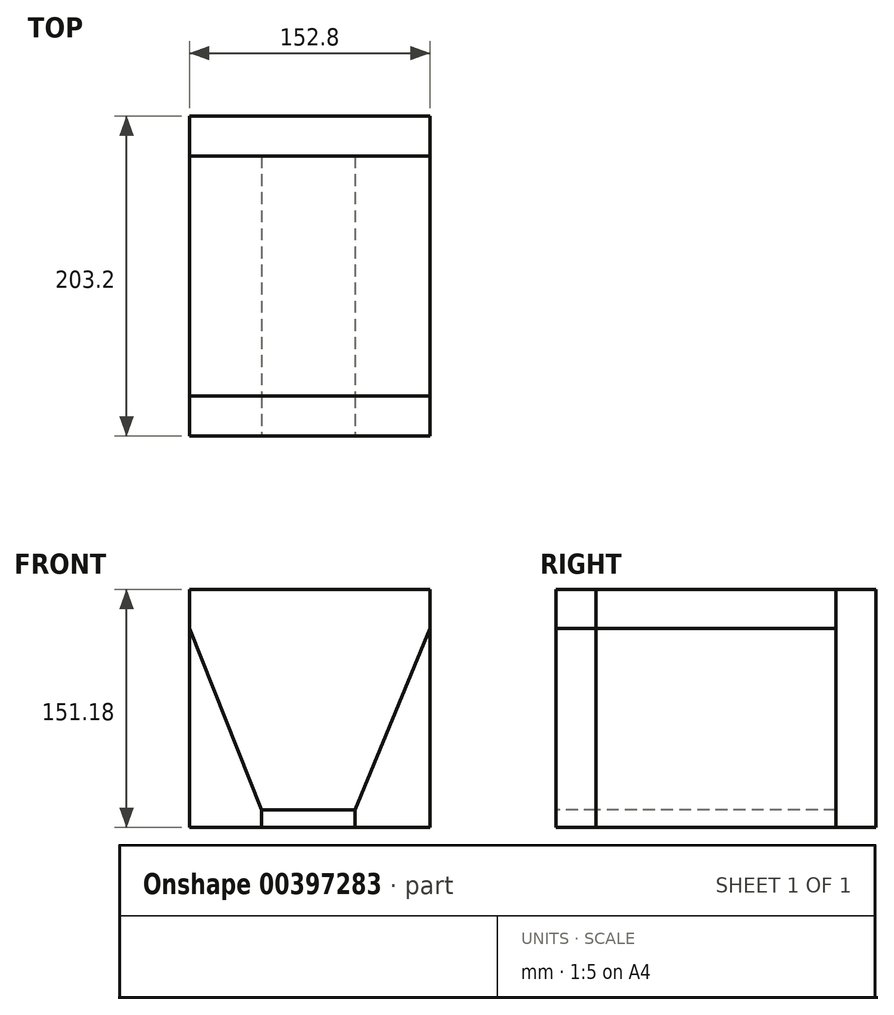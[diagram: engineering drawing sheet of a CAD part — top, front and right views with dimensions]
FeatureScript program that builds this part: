
annotation { "Feature Type Name" : "Feature", "Feature Type Description" : "" }
export const myFeature = defineFeature(function(context is Context, id is Id, definition is map)
    precondition{}
    {
        {
            var Q0;
            Q0=qCreatedBy(makeId("Front.planeOp"),FACE);
            var sketch = newSketch(context, id + "F0", { "sketchPlane" : qUnion([Q0])});
            skLineSegment(sketch, "E0.bottom", {"start": v(-76.38, 75.79) * mm, "end": v(76.38, 75.79) * mm});
            skLineSegment(sketch, "E0.top", {"start": v(-76.38, -75.4) * mm, "end": v(76.38, -75.4) * mm});
            skLineSegment(sketch, "E0.left", {"start": v(-76.38, 75.79) * mm, "end": v(-76.38, -75.4) * mm});
            skLineSegment(sketch, "E0.right", {"start": v(76.38, 75.79) * mm, "end": v(76.38, -75.4) * mm});
            skSolve(sketch);
        }
        {
            var Q0;
            Q0=makeQuery(id+"F0.imprint","IMPRINT",FACE,{"disambiguationData":[TD([[makeQuery(id+"F0.imprint","IMPRINT",EDGE,{"derivedFrom":sQuery(id+"F0.wireOp",EDGE,"E0.bottom")}),-1.0]])]});
            extrude(context, id + "F1", {"entities" : qUnion([Q0]), "depth" : 152.4 * mm});
        }
        {
            var Q0;
            Q0=makeQuery(id+"F1.opExtrude","CAP_FACE",FACE,{"disambiguationData":[OSD([sQuery(id+"F0.wireOp",EDGE,"E0.bottom"),sQuery(id+"F0.wireOp",EDGE,"E0.top"),sQuery(id+"F0.wireOp",EDGE,"E0.left"),sQuery(id+"F0.wireOp",EDGE,"E0.right")])],"isStart":false});
            var sketch = newSketch(context, id + "F2", { "sketchPlane" : qUnion([Q0])});
            skLineSegment(sketch, "E1.bottom", {"start": v(-76.38, 75.79) * mm, "end": v(76.38, 75.79) * mm});
            skLineSegment(sketch, "E1.top", {"start": v(-76.38, 50.96) * mm, "end": v(76.38, 50.96) * mm});
            skLineSegment(sketch, "E1.left", {"start": v(-76.38, 75.79) * mm, "end": v(-76.38, 50.96) * mm});
            skLineSegment(sketch, "E1.right", {"start": v(76.38, 75.79) * mm, "end": v(76.38, 50.96) * mm});
            skSolve(sketch);
        }
        {
            var Q0;
            Q0=makeQuery(id+"F2.imprint","IMPRINT",FACE,{"disambiguationData":[TD([[makeQuery(id+"F2.imprint","IMPRINT",EDGE,{"derivedFrom":sQuery(id+"F2.wireOp",EDGE,"E1.bottom")}),-1.0]])]});
            extrude(context, id + "F3", {"entities" : qUnion([Q0]), "operationType" : NewBodyOperationType.ADD, "depth" : 25.4 * mm});
        }
        {
            var Q0;
            Q0=makeQuery(id+"F1.opExtrude","CAP_FACE",FACE,{"disambiguationData":[OSD([sQuery(id+"F0.wireOp",EDGE,"E0.bottom"),sQuery(id+"F0.wireOp",EDGE,"E0.top"),sQuery(id+"F0.wireOp",EDGE,"E0.left"),sQuery(id+"F0.wireOp",EDGE,"E0.right")])],"isStart":false});
            var sketch = newSketch(context, id + "F4", { "sketchPlane" : qUnion([Q0])});
            skLineSegment(sketch, "E2.bottom", {"start": v(-30.79, -75.4) * mm, "end": v(28.6, -75.4) * mm});
            skLineSegment(sketch, "E2.top", {"start": v(-30.79, -64.33) * mm, "end": v(28.6, -64.33) * mm});
            skLineSegment(sketch, "E2.left", {"start": v(-30.79, -75.4) * mm, "end": v(-30.79, -64.33) * mm});
            skLineSegment(sketch, "E2.right", {"start": v(28.6, -75.4) * mm, "end": v(28.6, -64.33) * mm});
            skSolve(sketch);
        }
        {
            var Q0;
            Q0=makeQuery(id+"F4.imprint","IMPRINT",FACE,{"disambiguationData":[TD([[makeQuery(id+"F4.imprint","IMPRINT",EDGE,{"derivedFrom":sQuery(id+"F4.wireOp",EDGE,"E2.bottom")}),1.0]])]});
            extrude(context, id + "F5", {"entities" : qUnion([Q0]), "operationType" : NewBodyOperationType.ADD, "depth" : 25.4 * mm});
        }
        {
            var Q1;
            Q1=makeQuery(id+"F5.opExtrude","SWEPT_FACE",FACE,{"disambiguationData":[OSD([sQuery(id+"F4.wireOp",EDGE,"E2.top")])]});
            var Q2;
            Q2=makeQuery(id+"F3.opExtrude","SWEPT_FACE",FACE,{"disambiguationData":[OSD([sQuery(id+"F2.wireOp",EDGE,"E1.top")])]});
            loft(context, id + "F6", {"operationType" : NewBodyOperationType.ADD, "sheetProfilesArray" : [{ "sheetProfileEntities" : qUnion([Q1]) }, { "sheetProfileEntities" : qUnion([Q2]) }]});
        }
        {
            var Q0;
            {var subQ0=sQuery(id+"F4.wireOp",EDGE,"E2.top");var subQ1=sQuery(id+"F4.wireOp",EDGE,"E2.right");var subQ2=sQuery(id+"F4.wireOp",EDGE,"E2.left");var subQ3=sQuery(id+"F2.wireOp",EDGE,"E1.top");var subQ4=sQuery(id+"F2.wireOp",EDGE,"E1.right");var subQ5=sQuery(id+"F0.wireOp",EDGE,"E0.right");var subQ6=sQuery(id+"F2.wireOp",EDGE,"E1.left");var subQ7=sQuery(id+"F0.wireOp",EDGE,"E0.left");Q0=makeQuery(id+"F6.boolean.opBoolean","MERGE",FACE,{"derivedFrom":[makeQuery(id+"F3.opExtrude","CAP_FACE",FACE,{"disambiguationData":[OSD([sQuery(id+"F2.wireOp",EDGE,"E1.bottom"),subQ3,subQ6,subQ4])],"isStart":false}),makeQuery(id+"F5.opExtrude","CAP_FACE",FACE,{"disambiguationData":[OSD([sQuery(id+"F4.wireOp",EDGE,"E2.bottom"),subQ0,subQ2,subQ1])],"isStart":false}),makeQuery(id+"F6.opLoft","SWEPT_FACE",FACE,{"disambiguationData":[OSD([subQ7,subQ5,subQ3,subQ6,subQ4,subQ0,subQ2,subQ1]),TDD([makeQuery(id+"F3.opExtrude","CAP_VERTEX",VERTEX,{"disambiguationData":[OSD([subQ7,subQ3,subQ6])],"isStart":false}),makeQuery(id+"F3.opExtrude","CAP_VERTEX",VERTEX,{"disambiguationData":[OSD([subQ5,subQ3,subQ4])],"isStart":false}),makeQuery(id+"F3.opExtrude","CAP_EDGE",EDGE,{"disambiguationData":[OSD([subQ3])],"isStart":false}),makeQuery(id+"F5.opExtrude","CAP_VERTEX",VERTEX,{"disambiguationData":[OSD([subQ0,subQ2])],"isStart":false}),makeQuery(id+"F5.opExtrude","CAP_VERTEX",VERTEX,{"disambiguationData":[OSD([subQ0,subQ1])],"isStart":false}),makeQuery(id+"F5.opExtrude","CAP_EDGE",EDGE,{"disambiguationData":[OSD([subQ0])],"isStart":false})])]})]});}
            var sketch = newSketch(context, id + "F7", { "sketchPlane" : qUnion([Q0])});
            skSolve(sketch);
        }
        {
            var Q0;
            Q0=makeQuery(id+"F7.imprint","IMPRINT",FACE,{"disambiguationData":[TD([[makeQuery(id+"F7.imprint","IMPRINT",EDGE,{"derivedFrom":makeQuery(id+"F3.opExtrude","CAP_EDGE",EDGE,{"disambiguationData":[OSD([sQuery(id+"F2.wireOp",EDGE,"E1.bottom")])],"isStart":false})}),-1.0]])]});
            var sketch = newSketch(context, id + "F8", { "sketchPlane" : qUnion([Q0])});
            skLineSegment(sketch, "E3.bottom", {"start": v(-31, -64.33) * mm, "end": v(28.6, -64.33) * mm});
            skLineSegment(sketch, "E3.top", {"start": v(-31, 0) * mm, "end": v(28.6, 0) * mm});
            skLineSegment(sketch, "E3.left", {"start": v(-31, -64.33) * mm, "end": v(-31, 0) * mm});
            skLineSegment(sketch, "E3.right", {"start": v(28.6, -64.33) * mm, "end": v(28.6, 0) * mm});
            skSolve(sketch);
        }
        {
            var Q0;
            Q0=makeQuery(id+"F7.imprint","IMPRINT",FACE,{"disambiguationData":[TD([[makeQuery(id+"F7.imprint","IMPRINT",EDGE,{"derivedFrom":makeQuery(id+"F3.opExtrude","CAP_EDGE",EDGE,{"disambiguationData":[OSD([sQuery(id+"F2.wireOp",EDGE,"E1.bottom")])],"isStart":false})}),-1.0]])]});
            extrude(context, id + "F9", {"entities" : qUnion([Q0]), "operationType" : NewBodyOperationType.REMOVE, "endBound" : BoundingType.THROUGH_ALL, "oppositeDirection" : true, "depth" : 25.4 * mm});
        }
        {
            var Q0;
            {var subQ2=sQuery(id+"F8.wireOp",EDGE,"E3.top");Q0=makeQuery(id+"F8.imprint","IMPRINT",FACE,{"disambiguationData":[TD([[makeQuery(id+"F8.imprint","IMPRINT",EDGE,{"derivedFrom":subQ2}),-1.0]])]});}
            var Q1;
            {var subQ1=sQuery(id+"F8.wireOp",EDGE,"E3.top");Q1=makeQuery(id+"F8.imprint","IMPRINT",FACE,{"disambiguationData":[TD([[makeQuery(id+"F8.imprint","IMPRINT",EDGE,{"derivedFrom":subQ1}),1.0]])]});}
            extrude(context, id + "F10", {"entities" : qUnion([Q0, Q1]), "oppositeDirection" : true, "depth" : 25.4 * mm});
        }
        {
            var Q0;
            Q0=makeQuery(id+"F10.opExtrude","CAP_FACE",FACE,{"disambiguationData":[OSD([sQuery(id+"F0.wireOp",EDGE,"E0.left"),sQuery(id+"F0.wireOp",EDGE,"E0.right"),sQuery(id+"F2.wireOp",EDGE,"E1.bottom"),sQuery(id+"F2.wireOp",EDGE,"E1.top"),sQuery(id+"F2.wireOp",EDGE,"E1.left"),sQuery(id+"F2.wireOp",EDGE,"E1.right"),sQuery(id+"F4.wireOp",EDGE,"E2.top"),sQuery(id+"F4.wireOp",EDGE,"E2.left"),sQuery(id+"F4.wireOp",EDGE,"E2.right"),sQuery(id+"F8.wireOp",EDGE,"E3.bottom")])],"isStart":false});
            extrude(context, id + "F11", {"entities" : qUnion([Q0]), "depth" : 152.4 * mm});
        }
        {
            var Q0;
            Q0=makeQuery(id+"F11.opExtrude","CAP_FACE",FACE,{"disambiguationData":[OSD([sQuery(id+"F0.wireOp",EDGE,"E0.left"),sQuery(id+"F0.wireOp",EDGE,"E0.right"),sQuery(id+"F2.wireOp",EDGE,"E1.bottom"),sQuery(id+"F2.wireOp",EDGE,"E1.top"),sQuery(id+"F2.wireOp",EDGE,"E1.left"),sQuery(id+"F2.wireOp",EDGE,"E1.right"),sQuery(id+"F4.wireOp",EDGE,"E2.top"),sQuery(id+"F4.wireOp",EDGE,"E2.left"),sQuery(id+"F4.wireOp",EDGE,"E2.right"),sQuery(id+"F8.wireOp",EDGE,"E3.bottom")])],"isStart":false});
            var sketch = newSketch(context, id + "F12", { "sketchPlane" : qUnion([Q0])});
            skLineSegment(sketch, "E4.bottom", {"start": v(-76.38, 75.79) * mm, "end": v(76.42, 75.79) * mm});
            skLineSegment(sketch, "E4.top", {"start": v(-76.38, -75.24) * mm, "end": v(76.42, -75.24) * mm});
            skLineSegment(sketch, "E4.left", {"start": v(-76.38, 75.79) * mm, "end": v(-76.38, -75.24) * mm});
            skLineSegment(sketch, "E4.right", {"start": v(76.42, 75.79) * mm, "end": v(76.42, -75.24) * mm});
            skSolve(sketch);
        }
        {
            var Q0;
            Q0=makeQuery(id+"F12.imprint","IMPRINT",FACE,{"disambiguationData":[TD([[makeQuery(id+"F12.imprint","IMPRINT",EDGE,{"derivedFrom":makeQuery(id+"F11.opExtrude","CAP_EDGE",EDGE,{"disambiguationData":[OSD([sQuery(id+"F8.wireOp",EDGE,"E3.bottom")])],"isStart":false})}),-1.0]])]});
            var Q1;
            {var subQ5=sQuery(id+"F12.wireOp",EDGE,"E4.top");Q1=makeQuery(id+"F12.imprint","IMPRINT",FACE,{"disambiguationData":[TD([[makeQuery(id+"F12.imprint","IMPRINT",EDGE,{"derivedFrom":subQ5}),1.0]])]});}
            extrude(context, id + "F13", {"entities" : qUnion([Q0, Q1]), "depth" : 25.4 * mm});
        }
        {
            var Q0;
            Q0=makeQuery(id+"F9.boolean.opBoolean","COPY",FACE,{"derivedFrom":makeQuery(id+"F9.opExtrude","SWEPT_FACE",FACE,{"disambiguationData":[OSD([sQuery(id+"F4.wireOp",EDGE,"E2.left")])]})});
            var Q1;
            Q1=makeQuery(id+"F9.boolean.opBoolean","COPY",FACE,{"derivedFrom":makeQuery(id+"F9.opExtrude","SWEPT_FACE",FACE,{"disambiguationData":[OSD([sQuery(id+"F4.wireOp",EDGE,"E2.right")])]})});
            loft(context, id + "F14", {"sheetProfilesArray" : [{ "sheetProfileEntities" : qUnion([Q0]) }, { "sheetProfileEntities" : qUnion([Q1]) }]});
        }
        {
            var Q0;
            {var subQ1=sQuery(id+"F0.wireOp",EDGE,"E0.left");var subQ3=sQuery(id+"F0.wireOp",EDGE,"E0.top");Q0=makeQuery(id+"F6.boolean.opBoolean","SPLIT",FACE,{"disambiguationData":[TD([makeQuery(id+"F1.opExtrude","SWEPT_FACE",FACE,{"disambiguationData":[OSD([subQ1])]})])],"derivedFrom":makeQuery(id+"F1.opExtrude","CAP_FACE",FACE,{"disambiguationData":[OSD([sQuery(id+"F0.wireOp",EDGE,"E0.bottom"),subQ3,subQ1,sQuery(id+"F0.wireOp",EDGE,"E0.right")])],"isStart":false})});}
            var Q1;
            Q1=makeQuery(id+"F14.opLoft","SWEPT_FACE",FACE,{"disambiguationData":[OSD([sQuery(id+"F0.wireOp",EDGE,"E0.top"),sQuery(id+"F4.wireOp",EDGE,"E2.bottom"),sQuery(id+"F4.wireOp",EDGE,"E2.top"),sQuery(id+"F4.wireOp",EDGE,"E2.left"),sQuery(id+"F4.wireOp",EDGE,"E2.right")])]});
            extrude(context, id + "F15", {"entities" : qUnion([Q0, Q1]), "depth" : 25.4 * mm});
        }
        {
            var Q0;
            {var subQ1=sQuery(id+"F0.wireOp",EDGE,"E0.right");var subQ3=sQuery(id+"F0.wireOp",EDGE,"E0.top");Q0=makeQuery(id+"F6.boolean.opBoolean","SPLIT",FACE,{"disambiguationData":[TD([makeQuery(id+"F1.opExtrude","SWEPT_FACE",FACE,{"disambiguationData":[OSD([subQ1])]})])],"derivedFrom":makeQuery(id+"F1.opExtrude","CAP_FACE",FACE,{"disambiguationData":[OSD([sQuery(id+"F0.wireOp",EDGE,"E0.bottom"),subQ3,sQuery(id+"F0.wireOp",EDGE,"E0.left"),subQ1])],"isStart":false})});}
            extrude(context, id + "F16", {"entities" : qUnion([Q0]), "depth" : 25.4 * mm});
        }
    });
